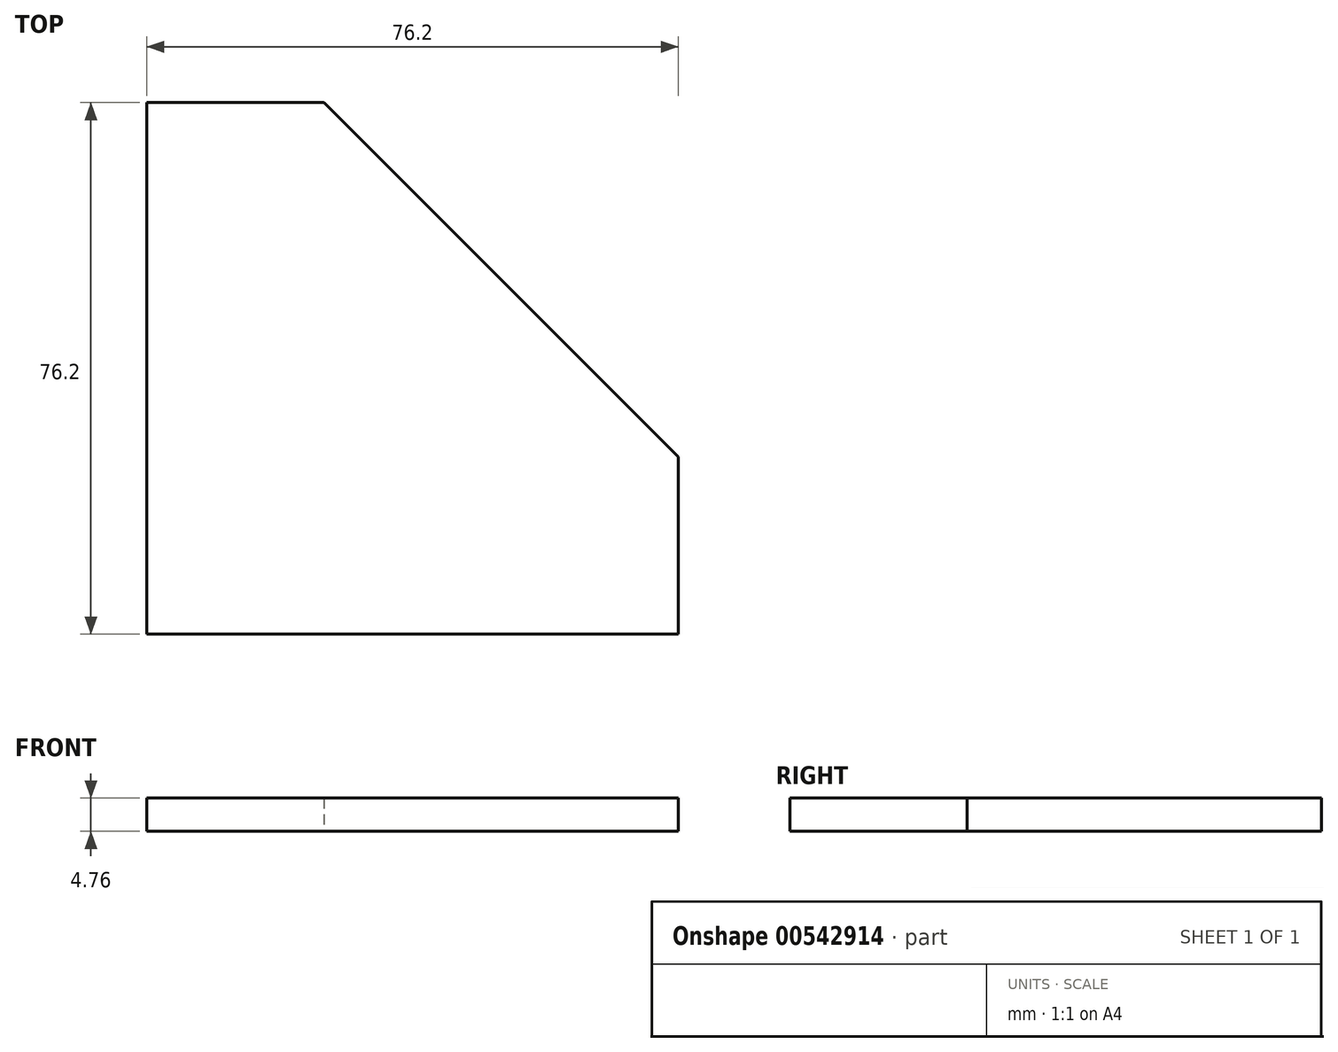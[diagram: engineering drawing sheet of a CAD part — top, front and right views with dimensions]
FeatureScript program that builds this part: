
annotation { "Feature Type Name" : "Feature", "Feature Type Description" : "" }
export const myFeature = defineFeature(function(context is Context, id is Id, definition is map)
    precondition{}
    {
        {
            var Q0;
            Q0=qCreatedBy(makeId("Top.planeOp"),FACE);
            var sketch = newSketch(context, id + "F0", { "sketchPlane" : qUnion([Q0])});
            skLineSegment(sketch, "E0", {"start": v(0, 0) * mm, "end": v(0, 76.2) * mm});
            skLineSegment(sketch, "E1", {"start": v(0, 0) * mm, "end": v(76.2, 0) * mm});
            skLineSegment(sketch, "E2", {"start": v(0, 76.2) * mm, "end": v(25.4, 76.2) * mm});
            skLineSegment(sketch, "E3", {"start": v(76.2, 0) * mm, "end": v(76.2, 25.4) * mm});
            skLineSegment(sketch, "E4", {"start": v(76.2, 25.4) * mm, "end": v(25.4, 76.2) * mm});
            skSolve(sketch);
        }
        {
            var Q0;
            Q0=makeQuery(id+"F0.imprint","IMPRINT",FACE,{"disambiguationData":[TD([[makeQuery(id+"F0.imprint","IMPRINT",EDGE,{"derivedFrom":sQuery(id+"F0.wireOp",EDGE,"E0")}),-1.0]])]});
            extrude(context, id + "F1", {"entities" : qUnion([Q0]), "depth" : 4.76 * mm, "offsetDistance" : 25.4 * mm});
        }
    });
